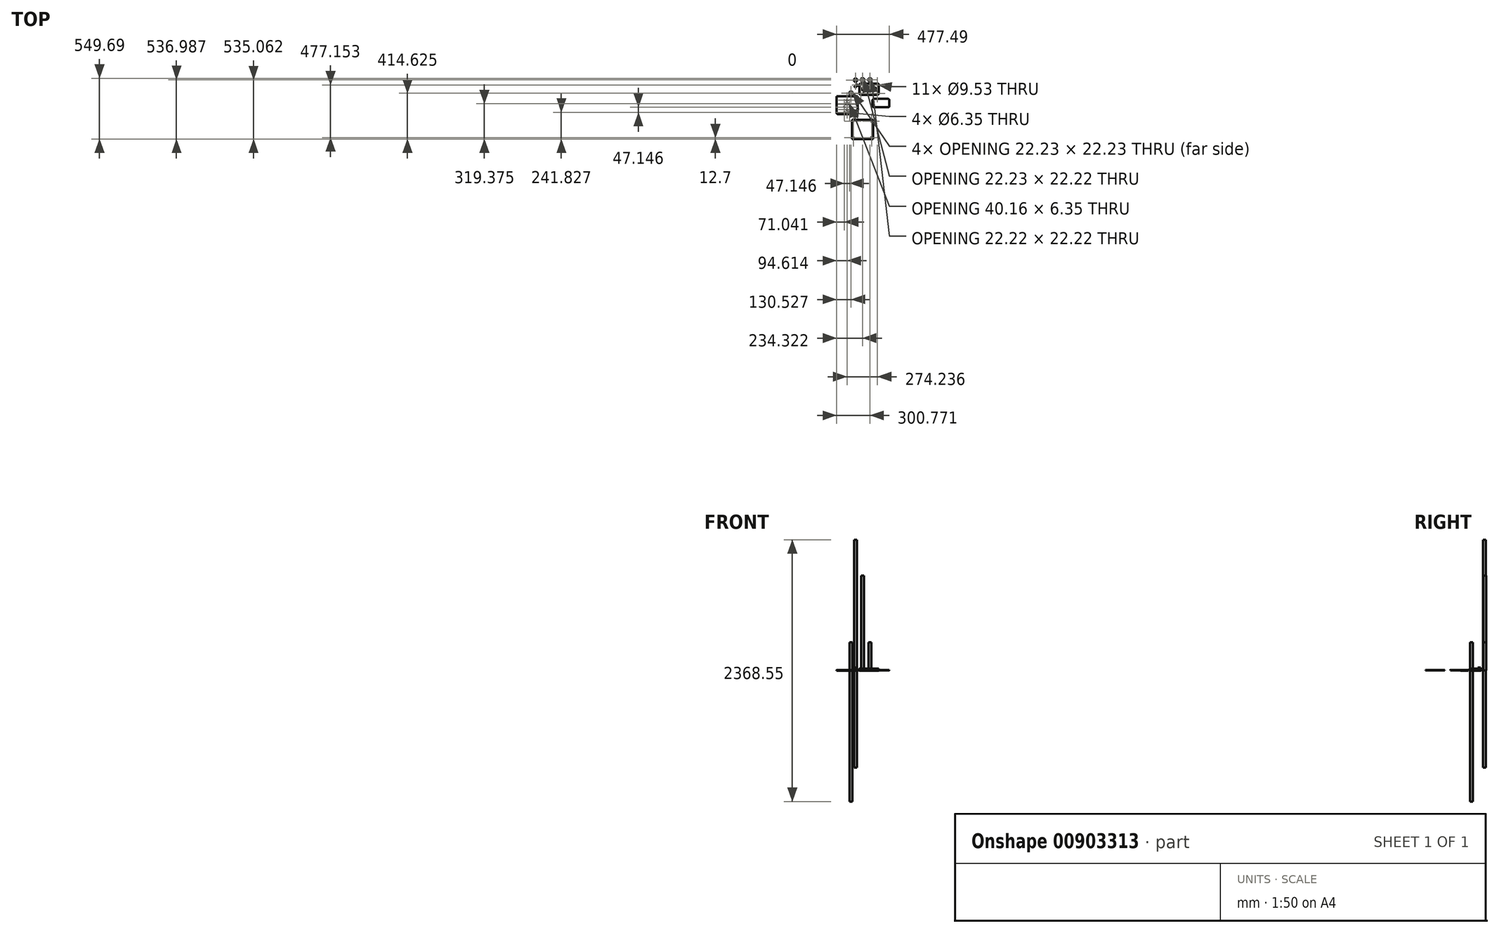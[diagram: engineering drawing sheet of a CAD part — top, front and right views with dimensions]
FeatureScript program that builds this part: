
annotation { "Feature Type Name" : "Feature", "Feature Type Description" : "" }
export const myFeature = defineFeature(function(context is Context, id is Id, definition is map)
    precondition{}
    {
        {
            var Q0;
            Q0=qCreatedBy(makeId("Top.planeOp"),FACE);
            var sketch = newSketch(context, id + "F0", { "sketchPlane" : qUnion([Q0])});
            skLineSegment(sketch, "E0.bottom", {"start": v(-56.72, 45.9) * mm, "end": v(-31.32, 45.9) * mm});
            skLineSegment(sketch, "E0.top", {"start": v(-56.72, 20.5) * mm, "end": v(-31.32, 20.5) * mm});
            skLineSegment(sketch, "E0.left", {"start": v(-56.72, 45.9) * mm, "end": v(-56.72, 20.5) * mm});
            skLineSegment(sketch, "E0.right", {"start": v(-31.32, 45.9) * mm, "end": v(-31.32, 20.5) * mm});
            skLineSegment(sketch, "E1.bottom", {"start": v(6.58, 46.4) * mm, "end": v(31.98, 46.4) * mm});
            skLineSegment(sketch, "E1.top", {"start": v(6.58, 21) * mm, "end": v(31.98, 21) * mm});
            skLineSegment(sketch, "E1.left", {"start": v(6.58, 46.4) * mm, "end": v(6.58, 21) * mm});
            skLineSegment(sketch, "E1.right", {"start": v(31.98, 46.4) * mm, "end": v(31.98, 21) * mm});
            skLineSegment(sketch, "E2", {"start": v(-33.96, -2.19) * mm, "end": v(-33.96, -21.24) * mm});
            skLineSegment(sketch, "E3", {"start": v(-37.14, -24.41) * mm, "end": v(-56.19, -24.41) * mm});
            skLineSegment(sketch, "E4", {"start": v(-56.19, -24.41) * mm, "end": v(-56.19, -27.59) * mm});
            skLineSegment(sketch, "E5", {"start": v(-56.19, -27.59) * mm, "end": v(-30.79, -27.59) * mm});
            skLineSegment(sketch, "E6", {"start": v(-30.79, -27.59) * mm, "end": v(-30.79, -2.19) * mm});
            skLineSegment(sketch, "E7", {"start": v(-30.79, -2.19) * mm, "end": v(-33.96, -2.19) * mm});
            skPoint(sketch, "E8.visualSharp", {"position": v(-33.96, -24.41) * mm});
            skArc(sketch, "E8.filletArc", {"start": v(-37.14, -24.41) * mm, "mid": v(-34.9, -23.48) * mm, "end": v(-33.96, -21.24) * mm});
            skLineSegment(sketch, "E9.0", {"start": v(-53.55, 44.32) * mm, "end": v(-34.5, 44.32) * mm});
            skLineSegment(sketch, "E9.1", {"start": v(-55.14, 42.73) * mm, "end": v(-55.14, 23.68) * mm});
            skLineSegment(sketch, "E9.2", {"start": v(-53.55, 22.1) * mm, "end": v(-34.5, 22.1) * mm});
            skLineSegment(sketch, "E9.3", {"start": v(-32.91, 42.73) * mm, "end": v(-32.91, 23.68) * mm});
            skPoint(sketch, "E10.visualSharp", {"position": v(-55.14, 44.32) * mm});
            skArc(sketch, "E10.filletArc", {"start": v(-53.55, 44.32) * mm, "mid": v(-54.67, 43.85) * mm, "end": v(-55.14, 42.73) * mm});
            skPoint(sketch, "E11.visualSharp", {"position": v(-32.91, 44.32) * mm});
            skArc(sketch, "E11.filletArc", {"start": v(-32.91, 42.73) * mm, "mid": v(-33.38, 43.85) * mm, "end": v(-34.5, 44.32) * mm});
            skPoint(sketch, "E12.visualSharp", {"position": v(-32.91, 22.1) * mm});
            skArc(sketch, "E12.filletArc", {"start": v(-34.5, 22.1) * mm, "mid": v(-33.38, 22.56) * mm, "end": v(-32.91, 23.68) * mm});
            skPoint(sketch, "E13.visualSharp", {"position": v(-55.14, 22.1) * mm});
            skArc(sketch, "E13.filletArc", {"start": v(-55.14, 23.68) * mm, "mid": v(-54.67, 22.56) * mm, "end": v(-53.55, 22.1) * mm});
            skLineSegment(sketch, "E14.0", {"start": v(30.4, 43.22) * mm, "end": v(30.4, 24.17) * mm});
            skLineSegment(sketch, "E14.1", {"start": v(9.76, 44.8) * mm, "end": v(28.8, 44.8) * mm});
            skLineSegment(sketch, "E14.2", {"start": v(8.17, 43.22) * mm, "end": v(8.17, 24.17) * mm});
            skLineSegment(sketch, "E14.3", {"start": v(9.76, 22.58) * mm, "end": v(28.8, 22.58) * mm});
            skPoint(sketch, "E15.visualSharp", {"position": v(8.17, 44.8) * mm});
            skArc(sketch, "E15.filletArc", {"start": v(9.76, 44.8) * mm, "mid": v(8.63, 44.34) * mm, "end": v(8.17, 43.22) * mm});
            skPoint(sketch, "E16.visualSharp", {"position": v(30.4, 44.8) * mm});
            skArc(sketch, "E16.filletArc", {"start": v(30.4, 43.22) * mm, "mid": v(29.93, 44.34) * mm, "end": v(28.8, 44.8) * mm});
            skPoint(sketch, "E17.visualSharp", {"position": v(30.4, 22.58) * mm});
            skArc(sketch, "E17.filletArc", {"start": v(28.8, 22.58) * mm, "mid": v(29.93, 23.04) * mm, "end": v(30.4, 24.17) * mm});
            skPoint(sketch, "E18.visualSharp", {"position": v(8.17, 22.58) * mm});
            skArc(sketch, "E18.filletArc", {"start": v(8.17, 24.17) * mm, "mid": v(8.63, 23.04) * mm, "end": v(9.76, 22.58) * mm});
            skLineSegment(sketch, "E19.bottom", {"start": v(3.69, 1.18) * mm, "end": v(153.81, 1.18) * mm});
            skLineSegment(sketch, "E19.top", {"start": v(3.69, -100.42) * mm, "end": v(153.81, -100.42) * mm});
            skLineSegment(sketch, "E19.left", {"start": v(-9.01, -11.52) * mm, "end": v(-9.01, -87.72) * mm});
            skLineSegment(sketch, "E19.right", {"start": v(166.51, -11.52) * mm, "end": v(166.51, -87.72) * mm});
            skPoint(sketch, "E20.visualSharp", {"position": v(-9.01, 1.18) * mm});
            skArc(sketch, "E20.filletArc", {"start": v(3.69, 1.18) * mm, "mid": v(-5.3, -2.54) * mm, "end": v(-9.01, -11.52) * mm});
            skPoint(sketch, "E21.visualSharp", {"position": v(-9.01, -100.42) * mm});
            skArc(sketch, "E21.filletArc", {"start": v(-9.01, -87.72) * mm, "mid": v(-5.3, -96.7) * mm, "end": v(3.69, -100.42) * mm});
            skPoint(sketch, "E22.visualSharp", {"position": v(166.51, -100.42) * mm});
            skArc(sketch, "E22.filletArc", {"start": v(153.81, -100.42) * mm, "mid": v(162.8, -96.7) * mm, "end": v(166.51, -87.72) * mm});
            skPoint(sketch, "E23.visualSharp", {"position": v(166.51, 1.18) * mm});
            skArc(sketch, "E23.filletArc", {"start": v(166.51, -11.52) * mm, "mid": v(162.8, -2.54) * mm, "end": v(153.81, 1.18) * mm});
            skCircle(sketch, "E24", {"center": v(3.69, -11.52) * mm, "radius": 4.76 * mm});
            skCircle(sketch, "E25", {"center": v(3.69, -87.72) * mm, "radius": 4.76 * mm});
            skCircle(sketch, "E26", {"center": v(153.81, -11.52) * mm, "radius": 4.76 * mm});
            skCircle(sketch, "E27", {"center": v(153.81, -87.72) * mm, "radius": 4.76 * mm});
            skLineSegment(sketch, "E28", {"start": v(-9.01, -49.62) * mm, "end": v(166.51, -49.62) * mm, "construction": true});
            skLineSegment(sketch, "E29", {"start": v(-9.01, -48.03) * mm, "end": v(166.51, -48.03) * mm});
            skLineSegment(sketch, "E30", {"start": v(-9.01, -51.2) * mm, "end": v(166.51, -51.2) * mm});
            skLineSegment(sketch, "E31", {"start": v(9.8, -49.62) * mm, "end": v(27.77, -31.66) * mm});
            skLineSegment(sketch, "E32", {"start": v(27.77, -31.66) * mm, "end": v(45.73, -49.62) * mm});
            skLineSegment(sketch, "E33", {"start": v(45.73, -49.62) * mm, "end": v(27.77, -67.58) * mm});
            skLineSegment(sketch, "E34", {"start": v(27.77, -67.58) * mm, "end": v(9.8, -49.62) * mm});
            skLineSegment(sketch, "E35", {"start": v(111.77, -49.62) * mm, "end": v(129.73, -31.66) * mm});
            skLineSegment(sketch, "E36", {"start": v(129.73, -31.66) * mm, "end": v(147.69, -49.62) * mm});
            skLineSegment(sketch, "E37", {"start": v(147.69, -49.62) * mm, "end": v(129.73, -67.58) * mm});
            skLineSegment(sketch, "E38", {"start": v(129.73, -67.58) * mm, "end": v(111.77, -49.62) * mm});
            skLineSegment(sketch, "E39", {"start": v(6.58, 21) * mm, "end": v(31.98, 46.4) * mm, "construction": true});
            skLineSegment(sketch, "E40", {"start": v(-56.72, 45.9) * mm, "end": v(-31.32, 20.5) * mm, "construction": true});
            skLineSegment(sketch, "E41.bottom", {"start": v(73.03, 48.32) * mm, "end": v(98.43, 48.32) * mm});
            skLineSegment(sketch, "E41.top", {"start": v(73.03, 22.92) * mm, "end": v(98.43, 22.92) * mm});
            skLineSegment(sketch, "E41.left", {"start": v(73.03, 48.32) * mm, "end": v(73.03, 22.92) * mm});
            skLineSegment(sketch, "E41.right", {"start": v(98.43, 48.32) * mm, "end": v(98.43, 22.92) * mm});
            skLineSegment(sketch, "E42.0", {"start": v(76.2, 24.5) * mm, "end": v(95.26, 24.5) * mm});
            skLineSegment(sketch, "E42.1", {"start": v(74.62, 45.14) * mm, "end": v(74.62, 26.1) * mm});
            skLineSegment(sketch, "E42.2", {"start": v(76.2, 46.73) * mm, "end": v(95.26, 46.73) * mm});
            skLineSegment(sketch, "E42.3", {"start": v(96.84, 45.14) * mm, "end": v(96.84, 26.1) * mm});
            skPoint(sketch, "E43.visualSharp", {"position": v(74.62, 46.73) * mm});
            skArc(sketch, "E43.filletArc", {"start": v(76.2, 46.73) * mm, "mid": v(75.08, 46.26) * mm, "end": v(74.62, 45.14) * mm});
            skPoint(sketch, "E44.visualSharp", {"position": v(96.84, 24.5) * mm});
            skArc(sketch, "E44.filletArc", {"start": v(95.26, 24.5) * mm, "mid": v(96.38, 24.97) * mm, "end": v(96.84, 26.1) * mm});
            skPoint(sketch, "E45.visualSharp", {"position": v(74.62, 24.5) * mm});
            skArc(sketch, "E45.filletArc", {"start": v(74.62, 26.1) * mm, "mid": v(75.08, 24.97) * mm, "end": v(76.2, 24.5) * mm});
            skPoint(sketch, "E46.visualSharp", {"position": v(96.84, 46.73) * mm});
            skArc(sketch, "E46.filletArc", {"start": v(96.84, 45.14) * mm, "mid": v(96.38, 46.26) * mm, "end": v(95.26, 46.73) * mm});
            skLineSegment(sketch, "E47", {"start": v(73.03, 22.92) * mm, "end": v(98.43, 48.32) * mm, "construction": true});
            skLineSegment(sketch, "E48.bottom", {"start": v(-97.21, -74.04) * mm, "end": v(-71.81, -74.04) * mm});
            skLineSegment(sketch, "E48.top", {"start": v(-97.21, -99.44) * mm, "end": v(-71.81, -99.44) * mm});
            skLineSegment(sketch, "E48.left", {"start": v(-97.21, -74.04) * mm, "end": v(-97.21, -99.44) * mm});
            skLineSegment(sketch, "E48.right", {"start": v(-71.81, -74.04) * mm, "end": v(-71.81, -99.44) * mm});
            skLineSegment(sketch, "E49.0", {"start": v(-73.4, -77.22) * mm, "end": v(-73.4, -96.27) * mm});
            skLineSegment(sketch, "E49.1", {"start": v(-94.04, -75.63) * mm, "end": v(-74.99, -75.63) * mm});
            skLineSegment(sketch, "E49.2", {"start": v(-95.63, -77.22) * mm, "end": v(-95.63, -96.27) * mm});
            skLineSegment(sketch, "E49.3", {"start": v(-94.04, -97.86) * mm, "end": v(-74.99, -97.86) * mm});
            skPoint(sketch, "E50.visualSharp", {"position": v(-95.63, -75.63) * mm});
            skArc(sketch, "E50.filletArc", {"start": v(-94.04, -75.63) * mm, "mid": v(-95.16, -76.1) * mm, "end": v(-95.63, -77.22) * mm});
            skPoint(sketch, "E51.visualSharp", {"position": v(-73.4, -75.63) * mm});
            skArc(sketch, "E51.filletArc", {"start": v(-73.4, -77.22) * mm, "mid": v(-73.87, -76.1) * mm, "end": v(-74.99, -75.63) * mm});
            skPoint(sketch, "E52.visualSharp", {"position": v(-73.4, -97.86) * mm});
            skArc(sketch, "E52.filletArc", {"start": v(-74.99, -97.86) * mm, "mid": v(-73.87, -97.4) * mm, "end": v(-73.4, -96.27) * mm});
            skPoint(sketch, "E53.visualSharp", {"position": v(-95.63, -97.86) * mm});
            skArc(sketch, "E53.filletArc", {"start": v(-95.63, -96.27) * mm, "mid": v(-95.16, -97.4) * mm, "end": v(-94.04, -97.86) * mm});
            skLineSegment(sketch, "E54", {"start": v(27.77, -31.66) * mm, "end": v(27.77, -49.62) * mm, "construction": true});
            skLineSegment(sketch, "E55", {"start": v(78.75, 1.18) * mm, "end": v(78.75, -100.42) * mm, "construction": true});
            skLineSegment(sketch, "E56", {"start": v(27.77, -31.66) * mm, "end": v(45.73, -13.7) * mm, "construction": true});
            skCircle(sketch, "E57", {"center": v(-202.34, -199.46) * mm, "radius": 3.18 * mm});
            skCircle(sketch, "E58", {"center": v(-202.34, -145.48) * mm, "radius": 3.18 * mm});
            skCircle(sketch, "E59", {"center": v(-37.24, -199.46) * mm, "radius": 3.18 * mm});
            skCircle(sketch, "E60", {"center": v(-37.24, -145.48) * mm, "radius": 3.18 * mm});
            skLineSegment(sketch, "E61", {"start": v(-208.19, -150.24) * mm, "end": v(-32.66, -150.24) * mm, "construction": true});
            skLineSegment(sketch, "E62", {"start": v(-189.37, -150.24) * mm, "end": v(-171.4, -132.28) * mm});
            skLineSegment(sketch, "E63", {"start": v(-171.4, -132.28) * mm, "end": v(-153.45, -150.24) * mm});
            skLineSegment(sketch, "E64", {"start": v(-153.45, -150.24) * mm, "end": v(-171.4, -168.2) * mm});
            skLineSegment(sketch, "E65", {"start": v(-171.4, -168.2) * mm, "end": v(-189.37, -150.24) * mm});
            skLineSegment(sketch, "E66", {"start": v(-87.4, -150.24) * mm, "end": v(-69.45, -132.28) * mm});
            skLineSegment(sketch, "E67", {"start": v(-69.45, -132.28) * mm, "end": v(-51.48, -150.24) * mm});
            skLineSegment(sketch, "E68", {"start": v(-51.48, -150.24) * mm, "end": v(-69.45, -168.2) * mm});
            skLineSegment(sketch, "E69", {"start": v(-69.45, -168.2) * mm, "end": v(-87.4, -150.24) * mm});
            skLineSegment(sketch, "E70", {"start": v(-171.4, -132.28) * mm, "end": v(-171.4, -150.24) * mm, "construction": true});
            skLineSegment(sketch, "E71", {"start": v(-120.43, -34.72) * mm, "end": v(-120.43, -265.77) * mm, "construction": true});
            skLineSegment(sketch, "E72", {"start": v(-171.4, -132.28) * mm, "end": v(-157.94, -118.81) * mm, "construction": true});
            skLineSegment(sketch, "E73.bottom", {"start": v(122.75, -137.73) * mm, "end": v(249.75, -137.73) * mm});
            skLineSegment(sketch, "E73.top", {"start": v(122.75, -213.93) * mm, "end": v(249.75, -213.93) * mm});
            skLineSegment(sketch, "E73.left", {"start": v(110.05, -150.43) * mm, "end": v(110.05, -201.23) * mm});
            skLineSegment(sketch, "E73.right", {"start": v(262.45, -150.43) * mm, "end": v(262.45, -201.23) * mm});
            skPoint(sketch, "E74.visualSharp", {"position": v(110.05, -137.73) * mm});
            skArc(sketch, "E74.filletArc", {"start": v(122.75, -137.73) * mm, "mid": v(113.77, -141.45) * mm, "end": v(110.05, -150.43) * mm});
            skPoint(sketch, "E75.visualSharp", {"position": v(110.05, -213.93) * mm});
            skArc(sketch, "E75.filletArc", {"start": v(110.05, -201.23) * mm, "mid": v(113.77, -210.21) * mm, "end": v(122.75, -213.93) * mm});
            skPoint(sketch, "E76.visualSharp", {"position": v(262.45, -213.93) * mm});
            skArc(sketch, "E76.filletArc", {"start": v(249.75, -213.93) * mm, "mid": v(258.73, -210.21) * mm, "end": v(262.45, -201.23) * mm});
            skPoint(sketch, "E77.visualSharp", {"position": v(262.45, -137.73) * mm});
            skArc(sketch, "E77.filletArc", {"start": v(262.45, -150.43) * mm, "mid": v(258.73, -141.45) * mm, "end": v(249.75, -137.73) * mm});
            skLineSegment(sketch, "E78", {"start": v(110.05, -175.83) * mm, "end": v(262.45, -175.83) * mm, "construction": true});
            skLineSegment(sketch, "E79", {"start": v(117.31, -175.83) * mm, "end": v(135.27, -157.87) * mm});
            skLineSegment(sketch, "E80", {"start": v(135.27, -157.87) * mm, "end": v(153.23, -175.83) * mm});
            skLineSegment(sketch, "E81", {"start": v(153.23, -175.83) * mm, "end": v(135.27, -193.8) * mm});
            skLineSegment(sketch, "E82", {"start": v(135.27, -193.8) * mm, "end": v(117.31, -175.83) * mm});
            skLineSegment(sketch, "E83", {"start": v(219.27, -175.83) * mm, "end": v(237.23, -157.87) * mm});
            skLineSegment(sketch, "E84", {"start": v(237.23, -157.87) * mm, "end": v(255.2, -175.83) * mm});
            skLineSegment(sketch, "E85", {"start": v(255.2, -175.83) * mm, "end": v(237.23, -193.8) * mm});
            skLineSegment(sketch, "E86", {"start": v(237.23, -193.8) * mm, "end": v(219.27, -175.83) * mm});
            skLineSegment(sketch, "E87", {"start": v(135.27, -157.87) * mm, "end": v(135.27, -175.83) * mm, "construction": true});
            skLineSegment(sketch, "E88", {"start": v(186.25, -137.73) * mm, "end": v(186.25, -213.93) * mm, "construction": true});
            skLineSegment(sketch, "E89", {"start": v(135.27, -157.87) * mm, "end": v(148.74, -144.4) * mm, "construction": true});
            skPoint(sketch, "E90.middle", {"position": v(-120.43, -150.24) * mm});
            skLineSegment(sketch, "E91.bottom", {"start": v(-202.34, -115.32) * mm, "end": v(-37.24, -115.32) * mm});
            skLineSegment(sketch, "E91.top", {"start": v(-215.04, -185.17) * mm, "end": v(-24.54, -185.17) * mm});
            skLineSegment(sketch, "E91.left", {"start": v(-215.04, -124.84) * mm, "end": v(-215.04, -185.17) * mm});
            skLineSegment(sketch, "E91.right", {"start": v(-24.54, -124.84) * mm, "end": v(-24.54, -185.17) * mm});
            skLineSegment(sketch, "E92", {"start": v(-171.4, -168.2) * mm, "end": v(-157.94, -181.68) * mm, "construction": true});
            skLineSegment(sketch, "E93", {"start": v(-189.37, -150.24) * mm, "end": v(-202.84, -163.71) * mm, "construction": true});
            skLineSegment(sketch, "E94", {"start": v(-189.37, -150.24) * mm, "end": v(-202.84, -136.77) * mm, "construction": true});
            skLineSegment(sketch, "E95", {"start": v(-51.48, -150.24) * mm, "end": v(-33.52, -168.2) * mm, "construction": true});
            skLineSegment(sketch, "E96.top", {"start": v(-202.34, -277.24) * mm, "end": v(-37.24, -277.24) * mm});
            skLineSegment(sketch, "E96.left", {"start": v(-215.04, -185.17) * mm, "end": v(-215.04, -264.54) * mm});
            skLineSegment(sketch, "E96.right", {"start": v(-24.54, -185.17) * mm, "end": v(-24.54, -264.54) * mm});
            skCircle(sketch, "E97", {"center": v(-120.43, -235.97) * mm, "radius": 33.34 * mm, "construction": true});
            skCircle(sketch, "E98", {"center": v(-120.43, -235.97) * mm, "radius": 4.76 * mm});
            skLineSegment(sketch, "E99", {"start": v(-120.43, -235.97) * mm, "end": v(-144, -212.4) * mm, "construction": true});
            skLineSegment(sketch, "E100", {"start": v(-120.43, -235.97) * mm, "end": v(-96.85, -212.4) * mm, "construction": true});
            skLineSegment(sketch, "E101", {"start": v(-120.43, -235.97) * mm, "end": v(-96.85, -259.54) * mm, "construction": true});
            skLineSegment(sketch, "E102", {"start": v(-120.43, -235.97) * mm, "end": v(-144, -259.54) * mm, "construction": true});
            skCircle(sketch, "E103", {"center": v(-144, -212.4) * mm, "radius": 3.18 * mm});
            skCircle(sketch, "E104", {"center": v(-96.85, -212.4) * mm, "radius": 3.18 * mm});
            skCircle(sketch, "E105", {"center": v(-96.85, -259.54) * mm, "radius": 3.18 * mm});
            skCircle(sketch, "E106", {"center": v(-144, -259.54) * mm, "radius": 3.18 * mm});
            skCircle(sketch, "E107", {"center": v(69.96, -293.36) * mm, "radius": 22.48 * mm, "construction": true});
            skCircle(sketch, "E108", {"center": v(127.37, -287.81) * mm, "radius": 11.2 * mm, "construction": true});
            skCircle(sketch, "E109", {"center": v(-120.43, -150.24) * mm, "radius": 4.76 * mm});
            skPoint(sketch, "E110.visualSharp", {"position": v(-215.04, -115.32) * mm});
            skPoint(sketch, "E111.visualSharp", {"position": v(-24.54, -115.32) * mm});
            skPoint(sketch, "E112.visualSharp", {"position": v(-24.54, -277.24) * mm});
            skArc(sketch, "E112.filletArc", {"start": v(-37.24, -277.24) * mm, "mid": v(-28.26, -273.52) * mm, "end": v(-24.54, -264.54) * mm});
            skPoint(sketch, "E113.visualSharp", {"position": v(-215.04, -277.24) * mm});
            skArc(sketch, "E113.filletArc", {"start": v(-215.04, -264.54) * mm, "mid": v(-211.32, -273.52) * mm, "end": v(-202.34, -277.24) * mm});
            skCircle(sketch, "E114", {"center": v(-120.43, -213.74) * mm, "radius": 34.93 * mm});
            skLineSegment(sketch, "E115", {"start": v(-202.34, -115.32) * mm, "end": v(-215.04, -115.32) * mm});
            skLineSegment(sketch, "E116", {"start": v(-215.04, -124.84) * mm, "end": v(-215.04, -115.32) * mm});
            skLineSegment(sketch, "E117", {"start": v(-24.54, -124.84) * mm, "end": v(-24.54, -115.32) * mm});
            skLineSegment(sketch, "E118", {"start": v(-37.24, -115.32) * mm, "end": v(-24.54, -115.32) * mm});
            skLineSegment(sketch, "E119.bottom", {"start": v(-77.08, -325.86) * mm, "end": v(113.42, -325.86) * mm});
            skLineSegment(sketch, "E119.top", {"start": v(-77.08, -501.37) * mm, "end": v(113.42, -501.37) * mm});
            skLineSegment(sketch, "E119.left", {"start": v(-77.08, -325.86) * mm, "end": v(-77.08, -501.37) * mm});
            skLineSegment(sketch, "E119.right", {"start": v(113.42, -325.86) * mm, "end": v(113.42, -501.37) * mm});
            skCircle(sketch, "E120", {"center": v(-64.38, -338.56) * mm, "radius": 4.76 * mm});
            skCircle(sketch, "E121", {"center": v(-64.38, -488.67) * mm, "radius": 4.76 * mm});
            skCircle(sketch, "E122", {"center": v(100.72, -338.56) * mm, "radius": 4.76 * mm});
            skCircle(sketch, "E123", {"center": v(100.72, -488.67) * mm, "radius": 4.76 * mm});
            skSolve(sketch);
        }
        {
            var Q0;
            Q0=makeQuery(id+"F0.imprint","IMPRINT",FACE,{"disambiguationData":[TD([[makeQuery(id+"F0.imprint","IMPRINT",EDGE,{"derivedFrom":sQuery(id+"F0.wireOp",EDGE,"E0.bottom")}),-1.0]])]});
            extrude(context, id + "F1", {"entities" : qUnion([Q0]), "depth" : 1181.1 * mm, "offsetDistance" : 25.4 * mm});
        }
        {
            var Q0;
            Q0=makeQuery(id+"F0.imprint","IMPRINT",FACE,{"disambiguationData":[TD([[makeQuery(id+"F0.imprint","IMPRINT",EDGE,{"derivedFrom":sQuery(id+"F0.wireOp",EDGE,"E1.bottom")}),-1.0]])]});
            extrude(context, id + "F2", {"entities" : qUnion([Q0]), "depth" : 856.62 * mm, "offsetDistance" : 25.4 * mm});
        }
        {
            var Q0;
            Q0=makeQuery(id+"F0.imprint","IMPRINT",FACE,{"disambiguationData":[TD([[makeQuery(id+"F0.imprint","IMPRINT",EDGE,{"derivedFrom":sQuery(id+"F0.wireOp",EDGE,"E2")}),1.0]])]});
            extrude(context, id + "F3", {"entities" : qUnion([Q0]), "depth" : 25.4 * mm, "offsetDistance" : 25.4 * mm});
        }
        {
            var Q0;
            Q0=makeQuery(id+"F0.imprint","IMPRINT",FACE,{"disambiguationData":[TD([[makeQuery(id+"F0.imprint","IMPRINT",EDGE,{"derivedFrom":sQuery(id+"F0.wireOp",EDGE,"E19.bottom")}),-1.0]])]});
            var Q1;
            Q1=makeQuery(id+"F0.imprint","IMPRINT",FACE,{"disambiguationData":[TD([[makeQuery(id+"F0.imprint","IMPRINT",EDGE,{"derivedFrom":sQuery(id+"F0.wireOp",EDGE,"E24")}),1.0]])]});
            var Q2;
            Q2=makeQuery(id+"F0.imprint","IMPRINT",FACE,{"disambiguationData":[TD([[makeQuery(id+"F0.imprint","IMPRINT",EDGE,{"derivedFrom":sQuery(id+"F0.wireOp",EDGE,"E26")}),1.0]])]});
            var Q3;
            Q3=makeQuery(id+"F0.imprint","IMPRINT",FACE,{"disambiguationData":[TD([[makeQuery(id+"F0.imprint","IMPRINT",EDGE,{"derivedFrom":sQuery(id+"F0.wireOp",EDGE,"E27")}),1.0]])]});
            var Q4;
            Q4=makeQuery(id+"F0.imprint","IMPRINT",FACE,{"disambiguationData":[TD([[makeQuery(id+"F0.imprint","IMPRINT",EDGE,{"derivedFrom":sQuery(id+"F0.wireOp",EDGE,"E19.top")}),1.0]])]});
            var Q5;
            Q5=makeQuery(id+"F0.imprint","IMPRINT",FACE,{"disambiguationData":[TD([[makeQuery(id+"F0.imprint","IMPRINT",EDGE,{"derivedFrom":sQuery(id+"F0.wireOp",EDGE,"E25")}),1.0]])]});
            extrude(context, id + "F4", {"entities" : qUnion([Q0, Q1, Q2, Q3, Q4, Q5]), "depth" : 15.88 * mm, "offsetDistance" : 25.4 * mm});
        }
        {
            var Q0;
            Q0=makeQuery(id+"F0.imprint","IMPRINT",FACE,{"disambiguationData":[TD([[makeQuery(id+"F0.imprint","IMPRINT",EDGE,{"derivedFrom":sQuery(id+"F0.wireOp",EDGE,"E19.bottom")}),-1.0]])]});
            var Q1;
            Q1=makeQuery(id+"F0.imprint","IMPRINT",FACE,{"disambiguationData":[TD([[makeQuery(id+"F0.imprint","IMPRINT",EDGE,{"derivedFrom":sQuery(id+"F0.wireOp",EDGE,"E19.top")}),1.0]])]});
            var Q2;
            {var subQ1=sQuery(id+"F0.wireOp",EDGE,"E32");var subQ9=sQuery(id+"F0.wireOp",EDGE,"E29");var subQ10=makeQuery(id+"F0.imprint","INTERSECT",VERTEX,{"derivedFrom":[subQ9,subQ1]});Q2=makeQuery(id+"F0.imprint","IMPRINT",FACE,{"disambiguationData":[TD([[makeQuery(id+"F0.imprint","IMPRINT",EDGE,{"disambiguationData":[TD([[subQ10,-1.0]])],"derivedFrom":subQ9}),-1.0]])]});}
            var Q3;
            {var subQ3=sQuery(id+"F0.wireOp",EDGE,"E29");var subQ6=sQuery(id+"F0.wireOp",EDGE,"E19.left");var subQ9=makeQuery(id+"F0.imprint","INTERSECT",VERTEX,{"derivedFrom":[subQ6,subQ3]});Q3=makeQuery(id+"F0.imprint","IMPRINT",FACE,{"disambiguationData":[TD([[makeQuery(id+"F0.imprint","IMPRINT",EDGE,{"disambiguationData":[TD([[subQ9,-1.0]])],"derivedFrom":subQ6}),1.0]])]});}
            var Q4;
            {var subQ3=sQuery(id+"F0.wireOp",EDGE,"E29");var subQ6=sQuery(id+"F0.wireOp",EDGE,"E19.right");var subQ9=makeQuery(id+"F0.imprint","INTERSECT",VERTEX,{"derivedFrom":[subQ6,subQ3]});Q4=makeQuery(id+"F0.imprint","IMPRINT",FACE,{"disambiguationData":[TD([[makeQuery(id+"F0.imprint","IMPRINT",EDGE,{"disambiguationData":[TD([[subQ9,-1.0]])],"derivedFrom":subQ6}),-1.0]])]});}
            var Q5;
            {var subQ0=sQuery(id+"F0.wireOp",EDGE,"E31");var subQ1=sQuery(id+"F0.wireOp",EDGE,"E29");var subQ2=makeQuery(id+"F0.imprint","INTERSECT",VERTEX,{"derivedFrom":[subQ1,subQ0]});Q5=makeQuery(id+"F0.imprint","IMPRINT",FACE,{"disambiguationData":[TD([[makeQuery(id+"F0.imprint","IMPRINT",EDGE,{"disambiguationData":[TD([[subQ2,-1.0]])],"derivedFrom":subQ1}),1.0]])]});}
            var Q6;
            {var subQ3=sQuery(id+"F0.wireOp",EDGE,"E29");var subQ6=sQuery(id+"F0.wireOp",EDGE,"E31");var subQ8=makeQuery(id+"F0.imprint","INTERSECT",VERTEX,{"derivedFrom":[subQ3,subQ6]});Q6=makeQuery(id+"F0.imprint","IMPRINT",FACE,{"disambiguationData":[TD([[makeQuery(id+"F0.imprint","IMPRINT",EDGE,{"disambiguationData":[TD([[subQ8,-1.0]])],"derivedFrom":subQ3}),-1.0]])]});}
            var Q7;
            {var subQ0=sQuery(id+"F0.wireOp",EDGE,"E34");var subQ1=sQuery(id+"F0.wireOp",EDGE,"E30");var subQ2=makeQuery(id+"F0.imprint","INTERSECT",VERTEX,{"derivedFrom":[subQ1,subQ0]});Q7=makeQuery(id+"F0.imprint","IMPRINT",FACE,{"disambiguationData":[TD([[makeQuery(id+"F0.imprint","IMPRINT",EDGE,{"disambiguationData":[TD([[subQ2,-1.0]])],"derivedFrom":subQ1}),-1.0]])]});}
            var Q8;
            {var subQ0=sQuery(id+"F0.wireOp",EDGE,"E38");var subQ1=sQuery(id+"F0.wireOp",EDGE,"E30");var subQ2=makeQuery(id+"F0.imprint","INTERSECT",VERTEX,{"derivedFrom":[subQ1,subQ0]});Q8=makeQuery(id+"F0.imprint","IMPRINT",FACE,{"disambiguationData":[TD([[makeQuery(id+"F0.imprint","IMPRINT",EDGE,{"disambiguationData":[TD([[subQ2,-1.0]])],"derivedFrom":subQ1}),-1.0]])]});}
            var Q9;
            {var subQ3=sQuery(id+"F0.wireOp",EDGE,"E29");var subQ6=sQuery(id+"F0.wireOp",EDGE,"E35");var subQ8=makeQuery(id+"F0.imprint","INTERSECT",VERTEX,{"derivedFrom":[subQ3,subQ6]});Q9=makeQuery(id+"F0.imprint","IMPRINT",FACE,{"disambiguationData":[TD([[makeQuery(id+"F0.imprint","IMPRINT",EDGE,{"disambiguationData":[TD([[subQ8,-1.0]])],"derivedFrom":subQ3}),-1.0]])]});}
            var Q10;
            {var subQ0=sQuery(id+"F0.wireOp",EDGE,"E35");var subQ1=sQuery(id+"F0.wireOp",EDGE,"E29");var subQ2=makeQuery(id+"F0.imprint","INTERSECT",VERTEX,{"derivedFrom":[subQ1,subQ0]});Q10=makeQuery(id+"F0.imprint","IMPRINT",FACE,{"disambiguationData":[TD([[makeQuery(id+"F0.imprint","IMPRINT",EDGE,{"disambiguationData":[TD([[subQ2,-1.0]])],"derivedFrom":subQ1}),1.0]])]});}
            extrude(context, id + "F5", {"entities" : qUnion([Q0, Q1, Q2, Q3, Q4, Q5, Q6, Q7, Q8, Q9, Q10]), "oppositeDirection" : true, "depth" : 3.17 * mm, "offsetDistance" : 25.4 * mm});
        }
        {
            var Q0;
            Q0=makeQuery(id+"F2.opExtrude","CAP_FACE",FACE,{"disambiguationData":[OSD([sQuery(id+"F0.wireOp",EDGE,"E1.bottom"),sQuery(id+"F0.wireOp",EDGE,"E1.top"),sQuery(id+"F0.wireOp",EDGE,"E1.left"),sQuery(id+"F0.wireOp",EDGE,"E1.right"),sQuery(id+"F0.wireOp",EDGE,"E14.0"),sQuery(id+"F0.wireOp",EDGE,"E14.1"),sQuery(id+"F0.wireOp",EDGE,"E14.2"),sQuery(id+"F0.wireOp",EDGE,"E14.3"),sQuery(id+"F0.wireOp",EDGE,"E15.filletArc"),sQuery(id+"F0.wireOp",EDGE,"E16.filletArc"),sQuery(id+"F0.wireOp",EDGE,"E17.filletArc"),sQuery(id+"F0.wireOp",EDGE,"E18.filletArc")])],"isStart":false});
            var sketch = newSketch(context, id + "F6", { "sketchPlane" : qUnion([Q0])});
            skLineSegment(sketch, "E124", {"start": v(6.58, 21) * mm, "end": v(31.98, 46.4) * mm, "construction": true});
            skSolve(sketch);
        }
        {
            var Q0;
            Q0=makeQuery(id+"F1.opExtrude","CAP_FACE",FACE,{"disambiguationData":[OSD([sQuery(id+"F0.wireOp",EDGE,"E0.bottom"),sQuery(id+"F0.wireOp",EDGE,"E0.top"),sQuery(id+"F0.wireOp",EDGE,"E0.left"),sQuery(id+"F0.wireOp",EDGE,"E0.right"),sQuery(id+"F0.wireOp",EDGE,"E9.0"),sQuery(id+"F0.wireOp",EDGE,"E9.1"),sQuery(id+"F0.wireOp",EDGE,"E9.2"),sQuery(id+"F0.wireOp",EDGE,"E9.3"),sQuery(id+"F0.wireOp",EDGE,"E10.filletArc"),sQuery(id+"F0.wireOp",EDGE,"E11.filletArc"),sQuery(id+"F0.wireOp",EDGE,"E12.filletArc"),sQuery(id+"F0.wireOp",EDGE,"E13.filletArc")])],"isStart":false});
            var sketch = newSketch(context, id + "F7", { "sketchPlane" : qUnion([Q0])});
            skLineSegment(sketch, "E125", {"start": v(-31.32, 20.5) * mm, "end": v(-56.72, 45.9) * mm, "construction": true});
            skLineSegment(sketch, "E126", {"start": v(-56.72, 20.5) * mm, "end": v(-31.32, 45.9) * mm, "construction": true});
            skSolve(sketch);
        }
        {
            var Q0;
            Q0=makeQuery(id+"F0.imprint","IMPRINT",FACE,{"disambiguationData":[TD([[makeQuery(id+"F0.imprint","IMPRINT",EDGE,{"derivedFrom":sQuery(id+"F0.wireOp",EDGE,"E41.bottom")}),-1.0]])]});
            extrude(context, id + "F8", {"entities" : qUnion([Q0]), "depth" : 254 * mm, "offsetDistance" : 25.4 * mm});
        }
        {
            var Q0;
            Q0=makeQuery(id+"F8.opExtrude","CAP_FACE",FACE,{"disambiguationData":[OSD([sQuery(id+"F0.wireOp",EDGE,"E41.bottom"),sQuery(id+"F0.wireOp",EDGE,"E41.top"),sQuery(id+"F0.wireOp",EDGE,"E41.left"),sQuery(id+"F0.wireOp",EDGE,"E41.right"),sQuery(id+"F0.wireOp",EDGE,"E42.0"),sQuery(id+"F0.wireOp",EDGE,"E42.1"),sQuery(id+"F0.wireOp",EDGE,"E42.2"),sQuery(id+"F0.wireOp",EDGE,"E42.3"),sQuery(id+"F0.wireOp",EDGE,"E43.filletArc"),sQuery(id+"F0.wireOp",EDGE,"E44.filletArc"),sQuery(id+"F0.wireOp",EDGE,"E45.filletArc"),sQuery(id+"F0.wireOp",EDGE,"E46.filletArc")])],"isStart":false});
            var sketch = newSketch(context, id + "F9", { "sketchPlane" : qUnion([Q0])});
            skLineSegment(sketch, "E127", {"start": v(73.03, 22.92) * mm, "end": v(98.43, 48.32) * mm, "construction": true});
            skSolve(sketch);
        }
        {
            var Q0;
            Q0=makeQuery(id+"F0.imprint","IMPRINT",FACE,{"disambiguationData":[TD([[makeQuery(id+"F0.imprint","IMPRINT",EDGE,{"derivedFrom":sQuery(id+"F0.wireOp",EDGE,"E48.bottom")}),-1.0]])]});
            extrude(context, id + "F10", {"entities" : qUnion([Q0]), "depth" : 254 * mm, "offsetDistance" : 25.4 * mm});
        }
        {
            var Q0;
            Q0=makeQuery(id+"F0.imprint","IMPRINT",FACE,{"disambiguationData":[TD([[makeQuery(id+"F0.imprint","IMPRINT",EDGE,{"derivedFrom":sQuery(id+"F0.wireOp",EDGE,"E48.bottom")}),-1.0]])]});
            extrude(context, id + "F11", {"entities" : qUnion([Q0]), "oppositeDirection" : true, "depth" : 1187.45 * mm, "offsetDistance" : 25.4 * mm});
        }
        {
            var Q0;
            Q0=makeQuery(id+"F0.imprint","IMPRINT",FACE,{"disambiguationData":[TD([[makeQuery(id+"F0.imprint","IMPRINT",EDGE,{"derivedFrom":sQuery(id+"F0.wireOp",EDGE,"E0.bottom")}),-1.0]])]});
            extrude(context, id + "F12", {"entities" : qUnion([Q0]), "oppositeDirection" : true, "depth" : 880.3 * mm, "offsetDistance" : 25.4 * mm});
        }
        {
            var Q0;
            Q0=makeQuery(id+"F0.imprint","IMPRINT",FACE,{"disambiguationData":[TD([[makeQuery(id+"F0.imprint","IMPRINT",EDGE,{"derivedFrom":sQuery(id+"F0.wireOp",EDGE,"E57")}),-1.0]])]});
            var Q1;
            Q1=makeQuery(id+"F0.imprint","IMPRINT",FACE,{"disambiguationData":[TD([[makeQuery(id+"F0.imprint","IMPRINT",EDGE,{"derivedFrom":sQuery(id+"F0.wireOp",EDGE,"E91.top")}),-1.0]])]});
            var Q2;
            Q2=makeQuery(id+"F0.imprint","IMPRINT",FACE,{"disambiguationData":[TD([[makeQuery(id+"F0.imprint","IMPRINT",EDGE,{"derivedFrom":sQuery(id+"F0.wireOp",EDGE,"E62")}),-1.0]])]});
            var Q3;
            Q3=makeQuery(id+"F0.imprint","IMPRINT",FACE,{"disambiguationData":[TD([[makeQuery(id+"F0.imprint","IMPRINT",EDGE,{"derivedFrom":sQuery(id+"F0.wireOp",EDGE,"E66")}),-1.0]])]});
            var Q4;
            Q4=makeQuery(id+"F0.imprint","IMPRINT",FACE,{"disambiguationData":[TD([[makeQuery(id+"F0.imprint","IMPRINT",EDGE,{"derivedFrom":sQuery(id+"F0.wireOp",EDGE,"E58")}),1.0]])]});
            var Q5;
            Q5=makeQuery(id+"F0.imprint","IMPRINT",FACE,{"disambiguationData":[TD([[makeQuery(id+"F0.imprint","IMPRINT",EDGE,{"derivedFrom":sQuery(id+"F0.wireOp",EDGE,"E57")}),1.0]])]});
            var Q6;
            Q6=makeQuery(id+"F0.imprint","IMPRINT",FACE,{"disambiguationData":[TD([[makeQuery(id+"F0.imprint","IMPRINT",EDGE,{"derivedFrom":sQuery(id+"F0.wireOp",EDGE,"E59")}),1.0]])]});
            var Q7;
            Q7=makeQuery(id+"F0.imprint","IMPRINT",FACE,{"disambiguationData":[TD([[makeQuery(id+"F0.imprint","IMPRINT",EDGE,{"derivedFrom":sQuery(id+"F0.wireOp",EDGE,"E58")}),-1.0]])]});
            var Q8;
            Q8=makeQuery(id+"F0.imprint","IMPRINT",FACE,{"disambiguationData":[TD([[makeQuery(id+"F0.imprint","IMPRINT",EDGE,{"derivedFrom":sQuery(id+"F0.wireOp",EDGE,"E60")}),1.0]])]});
            var Q9;
            {var subQ0=sQuery(id+"F0.wireOp",EDGE,"Dp7Box8H-mvKX-4fHT-27FS-wgEOYBGyVEAL");var subQ1=sQuery(id+"F0.wireOp",EDGE,"E91.bottom");var subQ2=makeQuery(id+"F0.imprint","INTERSECT",VERTEX,{"disambiguationData":[OD(0.0)],"derivedFrom":[subQ1,subQ0]});Q9=makeQuery(id+"F0.imprint","IMPRINT",FACE,{"disambiguationData":[TD([[makeQuery(id+"F0.imprint","IMPRINT",EDGE,{"disambiguationData":[TD([[subQ2,-1.0]])],"derivedFrom":subQ1}),-1.0]])]});}
            var Q10;
            Q10=makeQuery(id+"F0.imprint","IMPRINT",FACE,{"disambiguationData":[TD([[makeQuery(id+"F0.imprint","IMPRINT",EDGE,{"derivedFrom":sQuery(id+"F0.wireOp",EDGE,"E103")}),-1.0]])]});
            var Q11;
            {var subQ0=sQuery(id+"F0.wireOp",EDGE,"E114");var subQ1=sQuery(id+"F0.wireOp",EDGE,"E91.top");var subQ2=makeQuery(id+"F0.imprint","INTERSECT",VERTEX,{"disambiguationData":[OD(0.0)],"derivedFrom":[subQ1,subQ0]});Q11=makeQuery(id+"F0.imprint","IMPRINT",FACE,{"disambiguationData":[TD([[makeQuery(id+"F0.imprint","IMPRINT",EDGE,{"disambiguationData":[TD([[subQ2,-1.0]])],"derivedFrom":subQ1}),1.0]])]});}
            extrude(context, id + "F13", {"entities" : qUnion([Q0, Q1, Q2, Q3, Q4, Q5, Q6, Q7, Q8, Q9, Q10, Q11]), "depth" : 3.17 * mm, "offsetDistance" : 25.4 * mm});
        }
        {
            var Q0;
            Q0=makeQuery(id+"F0.imprint","IMPRINT",FACE,{"disambiguationData":[TD([[makeQuery(id+"F0.imprint","IMPRINT",EDGE,{"derivedFrom":sQuery(id+"F0.wireOp",EDGE,"E58")}),-1.0]])]});
            var Q1;
            Q1=makeQuery(id+"F0.imprint","IMPRINT",FACE,{"disambiguationData":[TD([[makeQuery(id+"F0.imprint","IMPRINT",EDGE,{"derivedFrom":sQuery(id+"F0.wireOp",EDGE,"E62")}),-1.0]])]});
            var Q2;
            Q2=makeQuery(id+"F0.imprint","IMPRINT",FACE,{"disambiguationData":[TD([[makeQuery(id+"F0.imprint","IMPRINT",EDGE,{"derivedFrom":sQuery(id+"F0.wireOp",EDGE,"E66")}),-1.0]])]});
            var Q3;
            Q3=makeQuery(id+"F0.imprint","IMPRINT",FACE,{"disambiguationData":[TD([[makeQuery(id+"F0.imprint","IMPRINT",EDGE,{"derivedFrom":sQuery(id+"F0.wireOp",EDGE,"E58")}),1.0]])]});
            var Q4;
            Q4=makeQuery(id+"F0.imprint","IMPRINT",FACE,{"disambiguationData":[TD([[makeQuery(id+"F0.imprint","IMPRINT",EDGE,{"derivedFrom":sQuery(id+"F0.wireOp",EDGE,"E60")}),1.0]])]});
            extrude(context, id + "F14", {"entities" : qUnion([Q0, Q1, Q2, Q3, Q4]), "oppositeDirection" : true, "depth" : 3.17 * mm, "offsetDistance" : 25.4 * mm});
        }
        {
            var Q0;
            Q0=makeQuery(id+"F0.imprint","IMPRINT",FACE,{"disambiguationData":[TD([[makeQuery(id+"F0.imprint","IMPRINT",EDGE,{"derivedFrom":sQuery(id+"F0.wireOp",EDGE,"E119.bottom")}),-1.0]])]});
            extrude(context, id + "F15", {"entities" : qUnion([Q0]), "depth" : 3.17 * mm, "offsetDistance" : 25.4 * mm});
        }
        {
            var Q0;
            Q0=makeQuery(id+"F0.imprint","IMPRINT",FACE,{"disambiguationData":[TD([[makeQuery(id+"F0.imprint","IMPRINT",EDGE,{"derivedFrom":sQuery(id+"F0.wireOp",EDGE,"E73.bottom")}),-1.0]])]});
            var Q1;
            Q1=makeQuery(id+"F0.imprint","IMPRINT",FACE,{"disambiguationData":[TD([[makeQuery(id+"F0.imprint","IMPRINT",EDGE,{"derivedFrom":sQuery(id+"F0.wireOp",EDGE,"E79")}),-1.0]])]});
            var Q2;
            Q2=makeQuery(id+"F0.imprint","IMPRINT",FACE,{"disambiguationData":[TD([[makeQuery(id+"F0.imprint","IMPRINT",EDGE,{"derivedFrom":sQuery(id+"F0.wireOp",EDGE,"E83")}),-1.0]])]});
            extrude(context, id + "F16", {"entities" : qUnion([Q0, Q1, Q2]), "depth" : 3.17 * mm, "offsetDistance" : 25.4 * mm});
        }
    });
